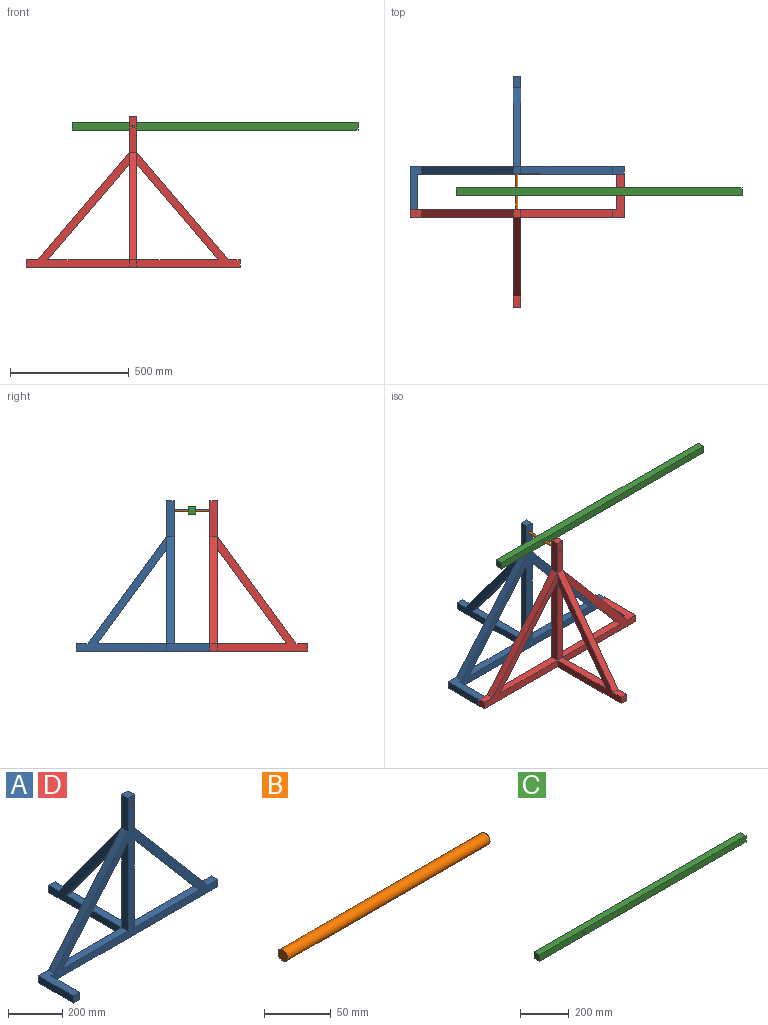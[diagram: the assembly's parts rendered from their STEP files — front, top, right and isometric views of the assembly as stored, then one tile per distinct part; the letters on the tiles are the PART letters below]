
ASSEMBLY  parts=4 mates=3
PART A: 29 faces, bbox 900x562x632 mm
  f0: plane 868x632mm, normal (0,-1,0), area 82684.2mm2, adj f5,f6,f7,f8,f9,f10,f12,f13
  f1: plane 395.89x32mm, normal (0,1,0), area 12668.4mm2, adj f4,f6,f8,f24
  f2: plane 482x434mm, normal (0,1,0), area 31781.4mm2, adj f7,f8,f9,f10,f14,f18,f19
  f3: plane 482x434mm, normal (0,1,0), area 31781.4mm2, adj f5,f6,f10,f12,f13,f20,f21
  f4: plane 290.32x32mm, normal (0,0,1), area 9290.2mm2, adj f1,f6,f8,f24
  f5: plane 341.93x32mm, normal (0,0,1), area 10941.8mm2, adj f0,f3,f6,f20
  f6: plane 482x412mm, normal (1,0,0), area 41765.9mm2, adj f0,f1,f3,f4,f5,f10,f20,f22
  f7: plane 182x50mm, normal (0,0,1), area 6400mm2, adj f0,f2,f14,f18,f26,f27
  f8: plane 482x412mm, normal (-1,0,0), area 41765.9mm2, adj f0,f1,f2,f4,f9,f10,f19,f22
  f9: plane 341.93x32mm, normal (0,0,1), area 10941.8mm2, adj f0,f2,f8,f19
  f10: plane 900x562mm, normal (0,0,-1), area 45760mm2, adj f0,f2,f3,f6,f8,f13,f14,f23
  f11: plane 150x32mm, normal (0,1,0), area 4721.5mm2, adj f15,f16,f17,f25,f28
  f12: plane 50x32mm, normal (0,0,1), area 1600mm2, adj f0,f3,f13,f21
  f13: plane 32x32mm, normal (1,0,0), area 1024mm2, adj f0,f3,f10,f12
  f14: plane 182x32mm, normal (-1,0,0), area 5824mm2, adj f2,f7,f10,f27
  f15: plane 150x32mm, normal (-1,0,0), area 4800mm2, adj f0,f11,f17,f18
  f16: plane 150x32mm, normal (1,0,0), area 4800mm2, adj f0,f11,f17,f21
  f17: plane 32x32mm, normal (0,0,1), area 1024mm2, adj f0,f11,f15,f16
  f18: plane 450x384mm, normal (-0.76,0,0.65), area 18930.3mm2, adj f0,f2,f7,f15
  f19: plane 400.7x341.93mm, normal (0.76,0,-0.65), area 16856.5mm2, adj f0,f2,f8,f9
  f20: plane 400.7x341.93mm, normal (-0.76,0,-0.65), area 16856.5mm2, adj f0,f3,f5,f6
  f21: plane 450x384mm, normal (0.76,0,0.65), area 18930.3mm2, adj f0,f3,f12,f16
  f22: plane 50x32mm, normal (0,0,1), area 1600mm2, adj f6,f8,f23,f25
  f23: plane 32x32mm, normal (0,1,0), area 1024mm2, adj f6,f8,f10,f22
  f24: plane 395.89x290.32mm, normal (0,-0.81,-0.59), area 15709.7mm2, adj f1,f4,f6,f8
  f25: plane 450x330mm, normal (0,0.81,0.59), area 17857mm2, adj f6,f8,f11,f22
  f26: plane 150x32mm, normal (1,0,0), area 4800mm2, adj f0,f7,f10,f27
  f27: plane 32x32mm, normal (0,-1,0), area 1024mm2, adj f7,f10,f14,f26
  f28: cylinder r=5mm len=32mm, axis (0,1,0), area 1005.3mm2, adj f0,f11
PART B: 3 faces, bbox 214x10x10 mm
  f0: cylinder r=5mm len=214mm, axis (-1,0,0), area 6723mm2, adj f1,f2
  f1: plane 10x10mm, normal (1,0,0), area 78.5mm2, adj f0
  f2: plane 10x10mm, normal (-1,0,0), area 78.5mm2, adj f0
PART C: 7 faces, bbox 1200x32x32 mm
  f0: plane 1200x32mm, normal (0,0,-1), area 38400mm2, adj f1,f3,f4,f5
  f1: plane 1200x32mm, normal (0,1,0), area 38321.5mm2, adj f0,f2,f4,f5,f6
  f2: plane 1200x32mm, normal (0,0,1), area 38400mm2, adj f1,f3,f4,f5
  f3: plane 1200x32mm, normal (0,-1,0), area 38321.5mm2, adj f0,f2,f4,f5,f6
  f4: plane 32x32mm, normal (1,0,0), area 1024mm2, adj f0,f1,f2,f3
  f5: plane 32x32mm, normal (-1,0,0), area 1024mm2, adj f0,f1,f2,f3
  f6: cylinder r=5mm len=32mm, axis (0,-1,0), area 1005.3mm2, adj f1,f3
PART D: same geometry as A
PLACE A t=(-2007.86,-19.07,-524.96)mm
PLACE B rot(axis=(0.58,0.58,0.58),120deg) t=(-2011.73,-233.07,73.66)mm
PLACE C t=(-2262.77,-110.07,51.16)mm
PLACE D rot(axis=(0,0,1),180deg) t=(-2007.86,-233.07,-524.96)mm
MATE fastened D.f28 <-> B.f0  axis (0,-1,0) through (-2007.86,-233.07,67.23)mm
MATE revolute B.f0 <-> C.f6  axis (0,-1,0) through (-2007.86,-126.07,67.23)mm
MATE fastened B.f0 <-> A.f28  axis (0,1,0) through (-2007.86,-19.07,67.23)mm
